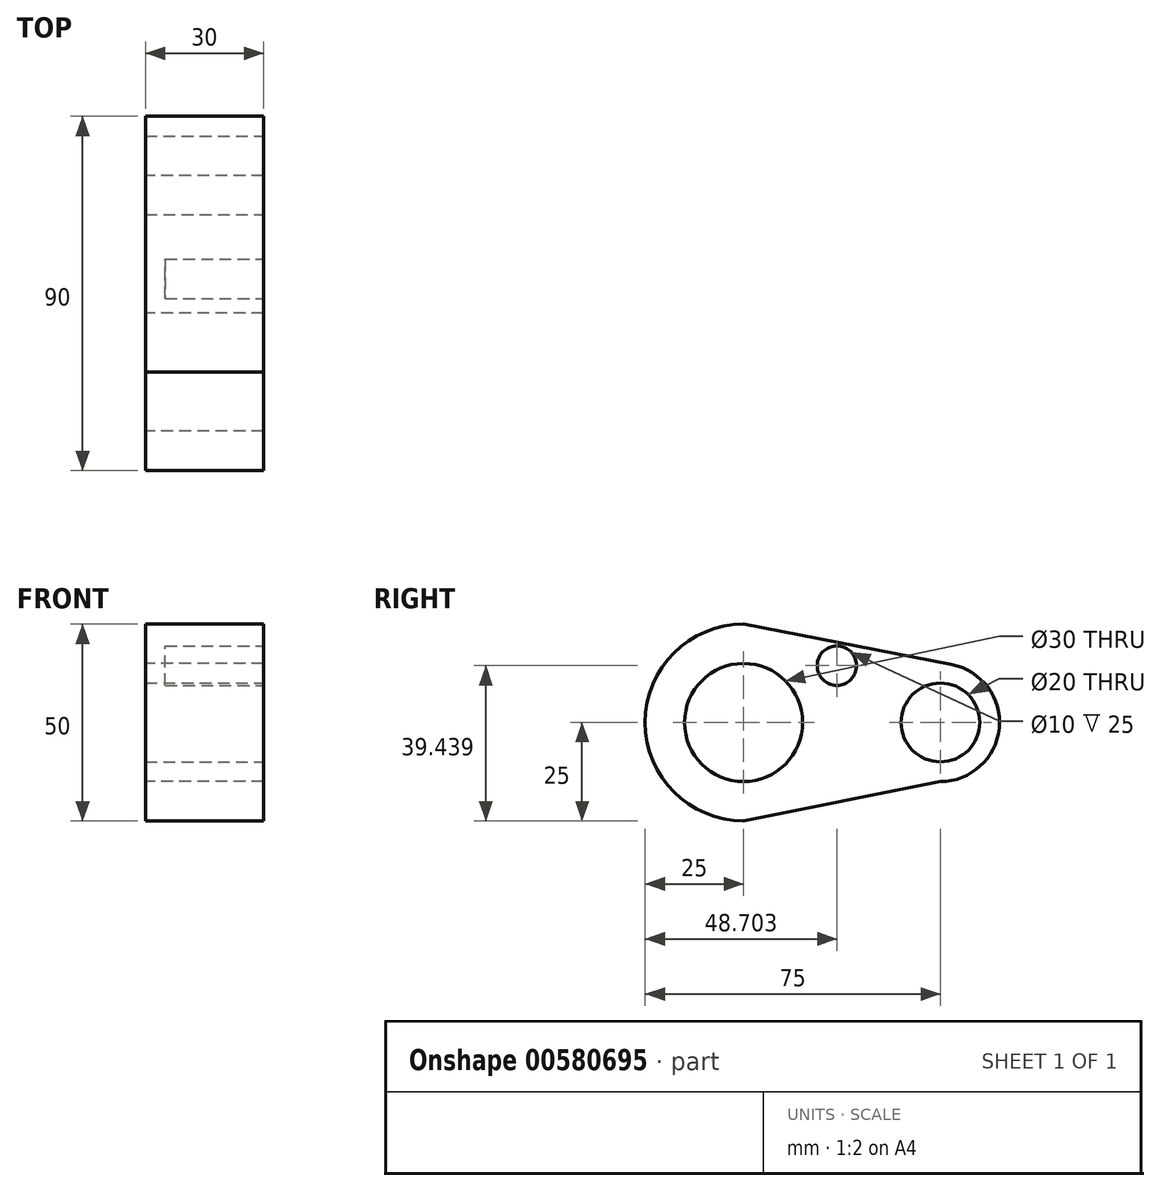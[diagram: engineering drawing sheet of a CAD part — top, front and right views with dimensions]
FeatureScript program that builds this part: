
annotation { "Feature Type Name" : "Feature", "Feature Type Description" : "" }
export const myFeature = defineFeature(function(context is Context, id is Id, definition is map)
    precondition{}
    {
        {
            var Q0;
            Q0=qCreatedBy(makeId("Right.planeOp"),FACE);
            var sketch = newSketch(context, id + "F0", { "sketchPlane" : qUnion([Q0])});
            skArc(sketch, "E0", {"start": v(0, 25) * mm, "mid": v(-25, 0) * mm, "end": v(0, -25) * mm});
            skArc(sketch, "E1", {"start": v(50, -15) * mm, "mid": v(64.93, -1.44) * mm, "end": v(52.86, 14.72) * mm});
            skLineSegment(sketch, "E2", {"start": v(0, 25) * mm, "end": v(52.86, 14.72) * mm});
            skLineSegment(sketch, "E3", {"start": v(0, -25) * mm, "end": v(50, -15) * mm});
            skCircle(sketch, "E4", {"center": v(0, 0) * mm, "radius": 15 * mm});
            skSolve(sketch);
        }
        {
            var Q0;
            Q0=makeQuery(id+"F0.imprint","IMPRINT",FACE,{"disambiguationData":[TD([[makeQuery(id+"F0.imprint","IMPRINT",EDGE,{"derivedFrom":sQuery(id+"F0.wireOp",EDGE,"E0")}),1.0]])]});
            extrude(context, id + "F1", {"entities" : qUnion([Q0]), "depth" : 30 * mm, "offsetDistance" : 25 * mm});
        }
        {
            var Q0;
            Q0=makeQuery(id+"F1.opExtrude","CAP_FACE",FACE,{"disambiguationData":[OSD([sQuery(id+"F0.wireOp",EDGE,"E0"),sQuery(id+"F0.wireOp",EDGE,"E1"),sQuery(id+"F0.wireOp",EDGE,"E2"),sQuery(id+"F0.wireOp",EDGE,"E3"),sQuery(id+"F0.wireOp",EDGE,"E4")])],"isStart":false});
            var sketch = newSketch(context, id + "F2", { "sketchPlane" : qUnion([Q0])});
            skCircle(sketch, "E5", {"center": v(50, 0) * mm, "radius": 10 * mm});
            skSolve(sketch);
        }
        {
            var Q0;
            Q0 = qSketchRegion(id + "F2", true);
            extrude(context, id + "F3", {"entities" : qUnion([Q0]), "operationType" : NewBodyOperationType.REMOVE, "endBound" : BoundingType.THROUGH_ALL, "oppositeDirection" : true, "depth" : 25 * mm, "offsetDistance" : 25 * mm});
        }
        {
            var Q0;
            Q0=makeQuery(id+"F1.opExtrude","CAP_FACE",FACE,{"disambiguationData":[OSD([sQuery(id+"F0.wireOp",EDGE,"E0"),sQuery(id+"F0.wireOp",EDGE,"E1"),sQuery(id+"F0.wireOp",EDGE,"E2"),sQuery(id+"F0.wireOp",EDGE,"E3"),sQuery(id+"F0.wireOp",EDGE,"E4")])],"isStart":false});
            var sketch = newSketch(context, id + "F4", { "sketchPlane" : qUnion([Q0])});
            skCircle(sketch, "E6", {"center": v(23.7, 14.44) * mm, "radius": 5 * mm});
            skSolve(sketch);
        }
        {
            var Q0;
            Q0 = qSketchRegion(id + "F4", true);
            extrude(context, id + "F5", {"entities" : qUnion([Q0]), "operationType" : NewBodyOperationType.REMOVE, "oppositeDirection" : true, "depth" : 25 * mm, "offsetDistance" : 25 * mm});
        }
    });
